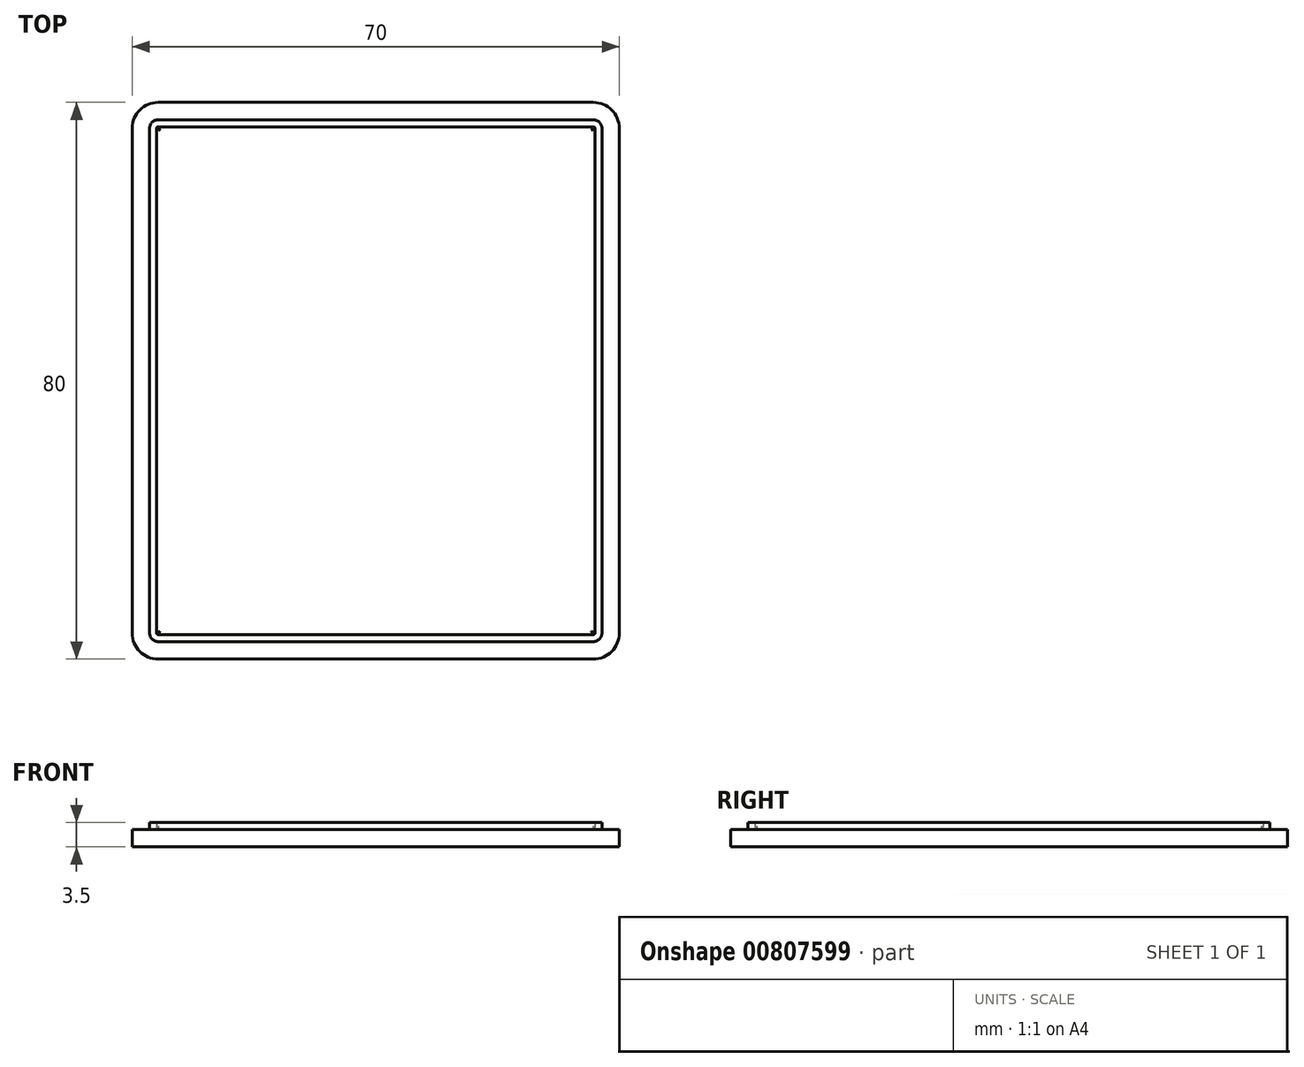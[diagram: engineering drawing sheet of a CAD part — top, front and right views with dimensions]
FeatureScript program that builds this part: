
annotation { "Feature Type Name" : "Feature", "Feature Type Description" : "" }
export const myFeature = defineFeature(function(context is Context, id is Id, definition is map)
    precondition{}
    {
        {
            var Q0;
            Q0=qCreatedBy(makeId("Top.planeOp"),FACE);
            var sketch = newSketch(context, id + "F0", { "sketchPlane" : qUnion([Q0])});
            skLineSegment(sketch, "E0.bottom", {"start": v(-36.84, 28.04) * mm, "end": v(33.16, 28.04) * mm});
            skLineSegment(sketch, "E0.top", {"start": v(-36.84, -51.96) * mm, "end": v(33.16, -51.96) * mm});
            skLineSegment(sketch, "E0.left", {"start": v(-36.84, 28.04) * mm, "end": v(-36.84, -51.96) * mm});
            skLineSegment(sketch, "E0.right", {"start": v(33.16, 28.04) * mm, "end": v(33.16, -51.96) * mm});
            skSolve(sketch);
        }
        {
            var Q0;
            Q0=makeQuery(id+"F0.imprint","IMPRINT",FACE,{"disambiguationData":[TD([[makeQuery(id+"F0.imprint","IMPRINT",EDGE,{"derivedFrom":sQuery(id+"F0.wireOp",EDGE,"E0.bottom")}),-1.0]])]});
            extrude(context, id + "F1", {"entities" : qUnion([Q0]), "depth" : 2.5 * mm, "offsetDistance" : 25 * mm});
        }
        {
            var Q0;
            Q0=makeQuery(id+"F1.opExtrude","CAP_FACE",FACE,{"disambiguationData":[OSD([sQuery(id+"F0.wireOp",EDGE,"E0.bottom"),sQuery(id+"F0.wireOp",EDGE,"E0.top"),sQuery(id+"F0.wireOp",EDGE,"E0.left"),sQuery(id+"F0.wireOp",EDGE,"E0.right")])],"isStart":false});
            var sketch = newSketch(context, id + "F2", { "sketchPlane" : qUnion([Q0])});
            skLineSegment(sketch, "E1.bottom", {"start": v(-34.34, 25.54) * mm, "end": v(30.66, 25.54) * mm});
            skLineSegment(sketch, "E1.top", {"start": v(-34.34, -49.46) * mm, "end": v(30.66, -49.46) * mm});
            skLineSegment(sketch, "E1.left", {"start": v(-34.34, 25.54) * mm, "end": v(-34.34, -49.46) * mm});
            skLineSegment(sketch, "E1.right", {"start": v(30.66, 25.54) * mm, "end": v(30.66, -49.46) * mm});
            skLineSegment(sketch, "E2.0", {"start": v(-33.34, 24.54) * mm, "end": v(29.66, 24.54) * mm});
            skLineSegment(sketch, "E2.1", {"start": v(-33.34, 24.54) * mm, "end": v(-33.34, -48.46) * mm});
            skLineSegment(sketch, "E2.2", {"start": v(-33.34, -48.46) * mm, "end": v(29.66, -48.46) * mm});
            skLineSegment(sketch, "E2.3", {"start": v(29.66, 24.54) * mm, "end": v(29.66, -48.46) * mm});
            skSolve(sketch);
        }
        {
            var Q0;
            Q0=makeQuery(id+"F2.imprint","IMPRINT",FACE,{"disambiguationData":[TD([[makeQuery(id+"F2.imprint","IMPRINT",EDGE,{"derivedFrom":sQuery(id+"F2.wireOp",EDGE,"E1.bottom")}),-1.0]])]});
            extrude(context, id + "F3", {"entities" : qUnion([Q0]), "operationType" : NewBodyOperationType.ADD, "depth" : 1 * mm, "offsetDistance" : 25 * mm});
        }
        {
            var Q0;
            Q0=makeQuery(id+"F1.opExtrude","SWEPT_EDGE",EDGE,{"disambiguationData":[OSD([sQuery(id+"F0.wireOp",EDGE,"E0.bottom"),sQuery(id+"F0.wireOp",EDGE,"E0.left")])]});
            var Q1;
            Q1=makeQuery(id+"F1.opExtrude","SWEPT_EDGE",EDGE,{"disambiguationData":[OSD([sQuery(id+"F0.wireOp",EDGE,"E0.bottom"),sQuery(id+"F0.wireOp",EDGE,"E0.right")])]});
            var Q2;
            Q2=makeQuery(id+"F1.opExtrude","SWEPT_EDGE",EDGE,{"disambiguationData":[OSD([sQuery(id+"F0.wireOp",EDGE,"E0.top"),sQuery(id+"F0.wireOp",EDGE,"E0.right")])]});
            var Q3;
            Q3=makeQuery(id+"F1.opExtrude","SWEPT_EDGE",EDGE,{"disambiguationData":[OSD([sQuery(id+"F0.wireOp",EDGE,"E0.top"),sQuery(id+"F0.wireOp",EDGE,"E0.left")])]});
            fillet(context, id + "F4", {"entities" : qUnion([Q0, Q1, Q2, Q3]), "radius" : 3.75 * mm, "tangentPropagation" : true, "allowEdgeOverflow" : false});
        }
        {
            var Q0;
            Q0=makeQuery(id+"F3.opExtrude","SWEPT_EDGE",EDGE,{"disambiguationData":[OSD([sQuery(id+"F2.wireOp",EDGE,"E1.top"),sQuery(id+"F2.wireOp",EDGE,"E1.left")])]});
            var Q1;
            Q1=makeQuery(id+"F3.opExtrude","SWEPT_EDGE",EDGE,{"disambiguationData":[OSD([sQuery(id+"F2.wireOp",EDGE,"E1.top"),sQuery(id+"F2.wireOp",EDGE,"E1.right")])]});
            var Q2;
            Q2=makeQuery(id+"F3.opExtrude","SWEPT_EDGE",EDGE,{"disambiguationData":[OSD([sQuery(id+"F2.wireOp",EDGE,"E1.bottom"),sQuery(id+"F2.wireOp",EDGE,"E1.right")])]});
            var Q3;
            Q3=makeQuery(id+"F3.opExtrude","SWEPT_EDGE",EDGE,{"disambiguationData":[OSD([sQuery(id+"F2.wireOp",EDGE,"E1.bottom"),sQuery(id+"F2.wireOp",EDGE,"E1.left")])]});
            fillet(context, id + "F5", {"entities" : qUnion([Q0, Q1, Q2, Q3]), "radius" : 1.25 * mm, "tangentPropagation" : true, "allowEdgeOverflow" : false});
        }
        {
            var Q0;
            Q0=makeQuery(id+"F3.opExtrude","SWEPT_EDGE",EDGE,{"disambiguationData":[OSD([sQuery(id+"F2.wireOp",EDGE,"E2.0"),sQuery(id+"F2.wireOp",EDGE,"E2.1")])]});
            var Q1;
            Q1=makeQuery(id+"F3.opExtrude","SWEPT_EDGE",EDGE,{"disambiguationData":[OSD([sQuery(id+"F2.wireOp",EDGE,"E2.0"),sQuery(id+"F2.wireOp",EDGE,"E2.3")])]});
            var Q2;
            Q2=makeQuery(id+"F3.opExtrude","SWEPT_EDGE",EDGE,{"disambiguationData":[OSD([sQuery(id+"F2.wireOp",EDGE,"E2.1"),sQuery(id+"F2.wireOp",EDGE,"E2.2")])]});
            var Q3;
            Q3=makeQuery(id+"F3.opExtrude","SWEPT_EDGE",EDGE,{"disambiguationData":[OSD([sQuery(id+"F2.wireOp",EDGE,"E2.2"),sQuery(id+"F2.wireOp",EDGE,"E2.3")])]});
            fillet(context, id + "F6", {"entities" : qUnion([Q0, Q1, Q2, Q3]), "radius" : 0.25 * mm, "tangentPropagation" : true, "allowEdgeOverflow" : false});
        }
        {
            var Q0;
            Q0=makeQuery(id+"F3.opExtrude","CAP_EDGE",EDGE,{"disambiguationData":[OSD([sQuery(id+"F2.wireOp",EDGE,"E1.top")])],"isStart":true});
            var Q1;
            Q1=makeQuery(id+"F3.opExtrude","CAP_EDGE",EDGE,{"disambiguationData":[OSD([sQuery(id+"F2.wireOp",EDGE,"E2.2")])],"isStart":true});
            fillet(context, id + "F7", {"entities" : qUnion([Q0, Q1]), "radius" : 0.5 * mm, "tangentPropagation" : true, "allowEdgeOverflow" : false});
        }
    });
